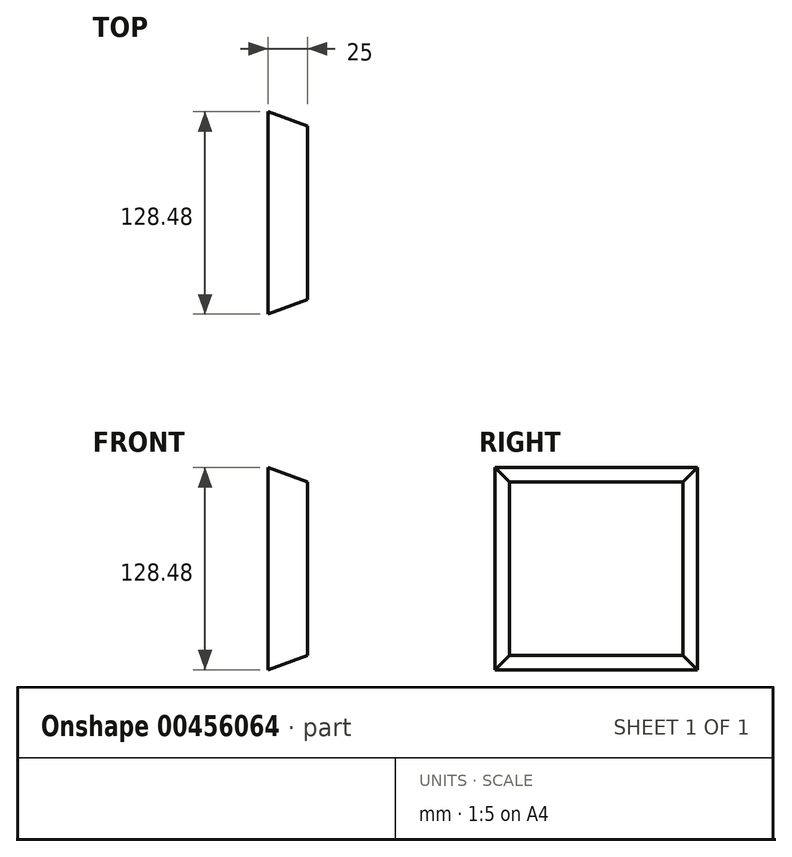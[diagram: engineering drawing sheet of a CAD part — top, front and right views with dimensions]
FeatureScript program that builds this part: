
annotation { "Feature Type Name" : "Feature", "Feature Type Description" : "" }
export const myFeature = defineFeature(function(context is Context, id is Id, definition is map)
    precondition{}
    {
        {
            var Q0;
            Q0=qCreatedBy(makeId("Right.planeOp"),FACE);
            var sketch = newSketch(context, id + "F0", { "sketchPlane" : qUnion([Q0])});
            skLineSegment(sketch, "E0.bottom", {"start": v(-102.62, 86.43) * mm, "end": v(27.66, 86.43) * mm});
            skLineSegment(sketch, "E0.top", {"start": v(-102.62, -43.85) * mm, "end": v(27.66, -43.85) * mm});
            skLineSegment(sketch, "E0.left", {"start": v(-102.62, 86.43) * mm, "end": v(-102.62, -43.85) * mm});
            skLineSegment(sketch, "E0.right", {"start": v(27.66, 86.43) * mm, "end": v(27.66, -43.85) * mm});
            skSolve(sketch);
        }
        {
            var Q0;
            Q0=makeQuery(id+"F0.imprint","IMPRINT",FACE,{"disambiguationData":[TD([[makeQuery(id+"F0.imprint","IMPRINT",EDGE,{"derivedFrom":sQuery(id+"F0.wireOp",EDGE,"E0.bottom")}),-1.0]])]});
            extrude(context, id + "F1", {"entities" : qUnion([Q0]), "depth" : 25 * mm});
        }
        {
            var Q0;
            Q0=makeQuery(id+"F1.opExtrude","CAP_EDGE",EDGE,{"disambiguationData":[OSD([sQuery(id+"F0.wireOp",EDGE,"E0.top")])],"isStart":false});
            var Q1;
            Q1=makeQuery(id+"F1.opExtrude","CAP_FACE",FACE,{"disambiguationData":[OSD([sQuery(id+"F0.wireOp",EDGE,"E0.bottom"),sQuery(id+"F0.wireOp",EDGE,"E0.top"),sQuery(id+"F0.wireOp",EDGE,"E0.left"),sQuery(id+"F0.wireOp",EDGE,"E0.right")])],"isStart":false});
            chamfer(context, id + "F2", {"entities" : qUnion([Q0, Q1]), "chamferType" : ChamferType.OFFSET_ANGLE, "width" : 10 * mm, "oppositeDirection" : false, "angle" : 70 * degree, "tangentPropagation" : true});
        }
    });
